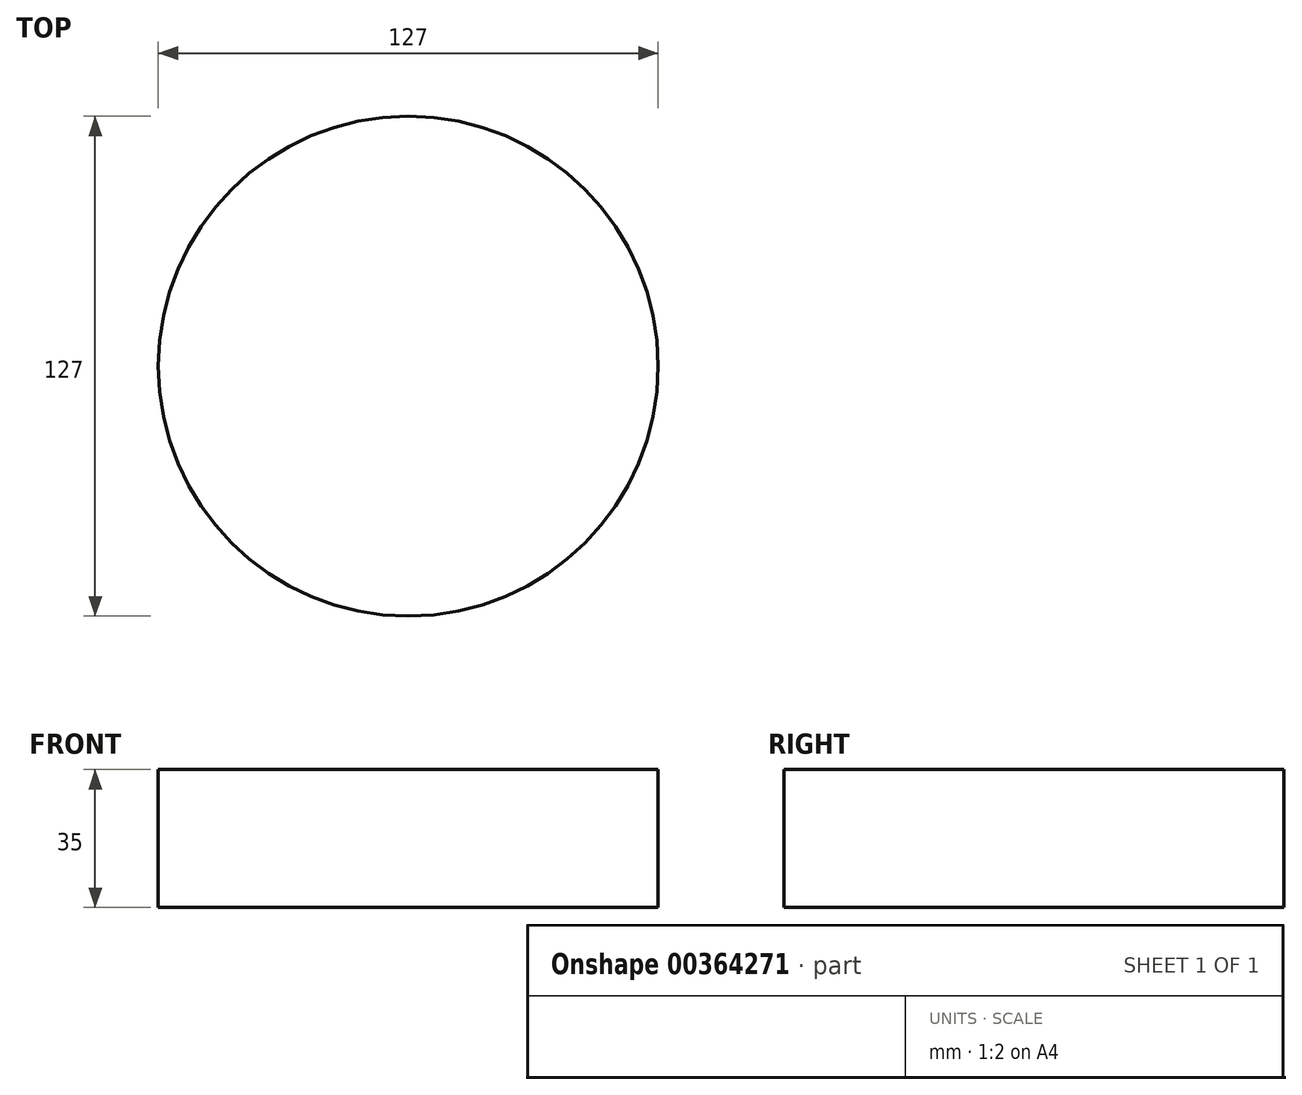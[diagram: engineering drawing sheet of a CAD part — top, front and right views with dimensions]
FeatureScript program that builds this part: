
annotation { "Feature Type Name" : "Feature", "Feature Type Description" : "" }
export const myFeature = defineFeature(function(context is Context, id is Id, definition is map)
    precondition{}
    {
        {
            var Q0;
            Q0=qCreatedBy(makeId("Top.planeOp"),FACE);
            var sketch = newSketch(context, id + "F0", { "sketchPlane" : qUnion([Q0])});
            skCircle(sketch, "E0", {"center": v(0, 0) * mm, "radius": 63.5 * mm});
            skSolve(sketch);
        }
        {
            var Q0;
            Q0=makeQuery(id+"F0.imprint","IMPRINT",FACE,{"disambiguationData":[TD([[makeQuery(id+"F0.imprint","IMPRINT",EDGE,{"derivedFrom":sQuery(id+"F0.wireOp",EDGE,"E0")}),1.0]])]});
            extrude(context, id + "F1", {"entities" : qUnion([Q0]), "depth" : 35 * mm});
        }
    });
